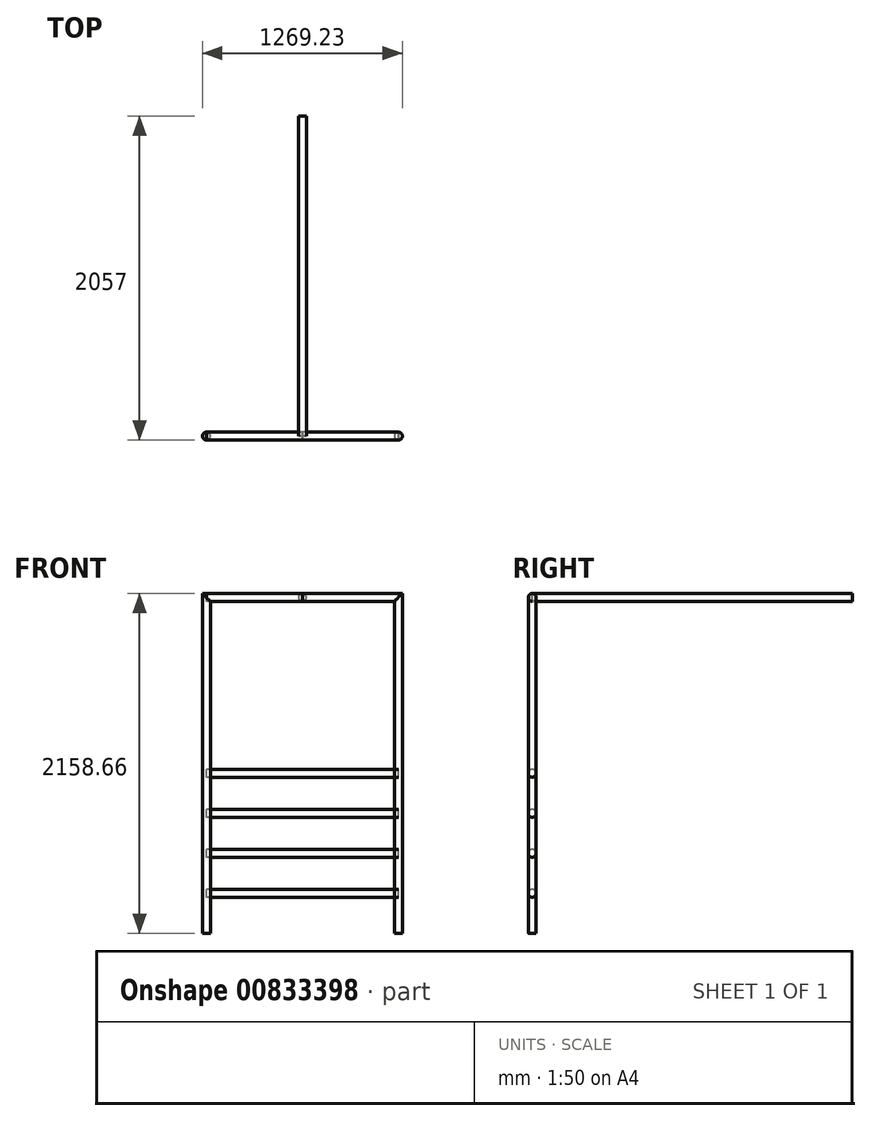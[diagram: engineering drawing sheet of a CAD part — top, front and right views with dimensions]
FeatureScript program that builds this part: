
annotation { "Feature Type Name" : "Feature", "Feature Type Description" : "" }
export const myFeature = defineFeature(function(context is Context, id is Id, definition is map)
    precondition{}
    {
        {
            var Q0;
            Q0=qCreatedBy(makeId("Top.planeOp"),FACE);
            var sketch = newSketch(context, id + "F0", { "sketchPlane" : qUnion([Q0])});
            skCircle(sketch, "E0", {"center": v(0, 0) * mm, "radius": 25 * mm});
            skSolve(sketch);
        }
        {
            var Q0;
            Q0=qCreatedBy(makeId("Front.planeOp"),FACE);
            var sketch = newSketch(context, id + "F1", { "sketchPlane" : qUnion([Q0])});
            skLineSegment(sketch, "E1", {"start": v(0, 0) * mm, "end": v(0, 2133.6) * mm});
            skLineSegment(sketch, "E2", {"start": v(0, 2133.6) * mm, "end": v(1219.2, 2133.6) * mm});
            skLineSegment(sketch, "E3", {"start": v(1219.2, 2133.6) * mm, "end": v(1219.2, 0) * mm});
            skLineSegment(sketch, "E4", {"start": v(0, 2133.6) * mm, "end": v(609.6, 2133.6) * mm});
            skLineSegment(sketch, "E5", {"start": v(0, 0) * mm, "end": v(0, 254) * mm});
            skLineSegment(sketch, "E6", {"start": v(0, 254) * mm, "end": v(0, 508) * mm});
            skLineSegment(sketch, "E7", {"start": v(0, 508) * mm, "end": v(0, 762) * mm});
            skLineSegment(sketch, "E8", {"start": v(0, 762) * mm, "end": v(0, 1016) * mm});
            skLineSegment(sketch, "E9", {"start": v(0, 1016) * mm, "end": v(1219.2, 1016) * mm});
            skPoint(sketch, "E9.endSnap0", {"position": v(1219.2, 1066.8) * mm});
            skLineSegment(sketch, "E10", {"start": v(0, 762) * mm, "end": v(1219.2, 762) * mm});
            skLineSegment(sketch, "E11", {"start": v(0, 508) * mm, "end": v(1219.2, 508) * mm});
            skLineSegment(sketch, "E12", {"start": v(0, 254) * mm, "end": v(1219.2, 254) * mm});
            skSolve(sketch);
        }
        {
            var Q0;
            Q0=qCreatedBy(makeId("Front.planeOp"),FACE);
            var sketch = newSketch(context, id + "F2", { "sketchPlane" : qUnion([Q0])});
            skPoint(sketch, "E13", {"position": v(609.57, 2133.66) * mm});
            skCircle(sketch, "E14", {"center": v(609.57, 2133.66) * mm, "radius": 25 * mm});
            skSolve(sketch);
        }
        {
            var Q0;
            Q0=makeQuery(id+"F2.imprint","IMPRINT",FACE,{"disambiguationData":[TD([[makeQuery(id+"F2.imprint","IMPRINT",EDGE,{"derivedFrom":sQuery(id+"F2.wireOp",EDGE,"E14")}),1.0]])]});
            extrude(context, id + "F3", {"entities" : qUnion([Q0]), "oppositeDirection" : true, "depth" : 2032 * mm, "offsetDistance" : 25.4 * mm});
        }
        {
            var Q0;
            Q0=makeQuery(id+"F0.imprint","IMPRINT",FACE,{"disambiguationData":[TD([[makeQuery(id+"F0.imprint","IMPRINT",EDGE,{"derivedFrom":sQuery(id+"F0.wireOp",EDGE,"E0")}),1.0]])]});
            var Q1;
            Q1=sQuery(id+"F1.wireOp",EDGE,"E1");
            var Q2;
            Q2=sQuery(id+"F1.wireOp",EDGE,"E4");
            sweep(context, id + "F4", {"profiles" : qUnion([Q0]), "path" : qUnion([Q1, Q2])});
        }
        {
            var Q0;
            Q0=sQuery(id+"F1.wireOp",VERTEX,"E3.end");
            var Q1;
            Q1=sQuery(id+"F1.wireOp",EDGE,"E3");
            cPlane(context, id + "F5", {"entities" : qUnion([Q0, Q1]), "cplaneType" : CPlaneType.LINE_POINT, "offset" : 25.4 * mm, "width" : 152.4 * mm, "height" : 152.4 * mm});
        }
        {
            var Q0;
            Q0=qCreatedBy(id+"F5.planeOp",FACE);
            var sketch = newSketch(context, id + "F6", { "sketchPlane" : qUnion([Q0])});
            skPoint(sketch, "E15", {"position": v(1219.23, 0) * mm});
            skCircle(sketch, "E16", {"center": v(1219.23, 0) * mm, "radius": 25 * mm});
            skSolve(sketch);
        }
        {
            var Q0;
            Q0=makeQuery(id+"F6.imprint","IMPRINT",FACE,{"disambiguationData":[TD([[makeQuery(id+"F6.imprint","IMPRINT",EDGE,{"derivedFrom":sQuery(id+"F6.wireOp",EDGE,"E16")}),1.0]])]});
            var Q1;
            Q1=sQuery(id+"F1.wireOp",EDGE,"E3");
            var Q2;
            Q2=sQuery(id+"F1.wireOp",EDGE,"E2");
            sweep(context, id + "F7", {"profiles" : qUnion([Q0]), "path" : qUnion([Q1, Q2])});
        }
        {
            var Q0;
            Q0=sQuery(id+"F1.wireOp",VERTEX,"E8.end");
            var Q1;
            Q1=sQuery(id+"F1.wireOp",EDGE,"E9");
            cPlane(context, id + "F8", {"entities" : qUnion([Q0, Q1]), "cplaneType" : CPlaneType.LINE_POINT, "offset" : 25.4 * mm, "width" : 152.4 * mm, "height" : 152.4 * mm});
        }
        {
            var Q0;
            Q0=qCreatedBy(id+"F8.planeOp",FACE);
            var sketch = newSketch(context, id + "F9", { "sketchPlane" : qUnion([Q0])});
            skCircle(sketch, "E17", {"center": v(0, 1016.6) * mm, "radius": 25 * mm});
            skCircle(sketch, "E18", {"center": v(0, 762) * mm, "radius": 25 * mm});
            skCircle(sketch, "E19", {"center": v(0, 508.09) * mm, "radius": 25 * mm});
            skCircle(sketch, "E20", {"center": v(0, 254.16) * mm, "radius": 25 * mm});
            skSolve(sketch);
        }
        {
            var Q0;
            Q0 = qSketchRegion(id + "F9", true);
            extrude(context, id + "F10", {"entities" : qUnion([Q0]), "depth" : 1219.2 * mm, "offsetDistance" : 25.4 * mm});
        }
    });
